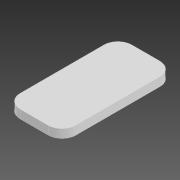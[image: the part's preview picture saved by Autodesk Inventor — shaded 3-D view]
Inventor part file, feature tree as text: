
AUTODESK INVENTOR PART (.ipt)
format: ipt  version: 2020 (Build 240168000, 168)  size: 84,480 bytes
history: native  units: in
note: dims shown in document units (in); Inventor stores cm internally (conversion verified against a paired STEP export)
features: extrude x1, fillet x1, sketch x1
ambient origin geometry x8: Origin, YZ Plane, XZ Plane, XY Plane, X Axis, Y Axis, Z Axis, Center Point
bodies: Solid1 (feature_tree)
feature tree (3):
  extrude  "Extrusion1"  Depth=1.5748in
  fillet  "Fillet1"  Radius=0.1181in
  sketch  "Sketch1"  dims[d0=0.7874in d1=1.5748in d2=0.1181in d3=0.0in d4=0.1969in]
